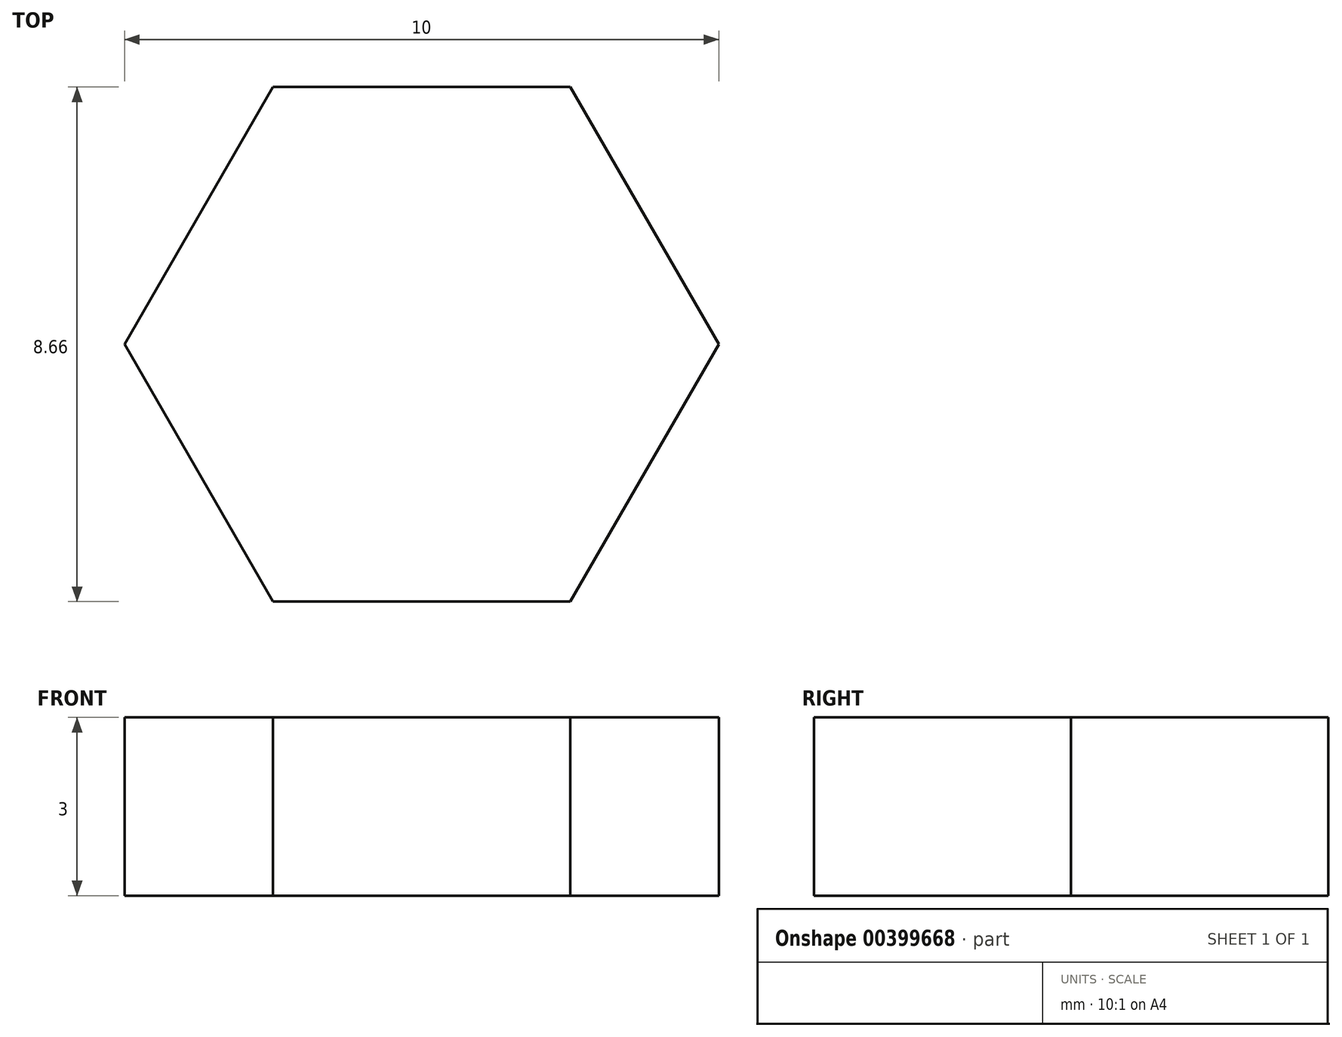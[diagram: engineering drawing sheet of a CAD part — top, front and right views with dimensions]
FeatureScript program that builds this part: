
annotation { "Feature Type Name" : "Feature", "Feature Type Description" : "" }
export const myFeature = defineFeature(function(context is Context, id is Id, definition is map)
    precondition{}
    {
        {
            var Q0;
            Q0=qCreatedBy(makeId("Top.planeOp"),FACE);
            var sketch = newSketch(context, id + "F0", { "sketchPlane" : qUnion([Q0])});
            skCircle(sketch, "E0.cCircle", {"center": v(0, 0) * mm, "radius": 4.33 * mm, "construction": true});
            skLineSegment(sketch, "E0.0", {"start": v(2.5, 4.33) * mm, "end": v(5, 0) * mm});
            skLineSegment(sketch, "E0.1", {"start": v(5, 0) * mm, "end": v(2.5, -4.33) * mm});
            skLineSegment(sketch, "E0.2", {"start": v(2.5, -4.33) * mm, "end": v(-2.5, -4.33) * mm});
            skLineSegment(sketch, "E0.3", {"start": v(-2.5, -4.33) * mm, "end": v(-5, 0) * mm});
            skLineSegment(sketch, "E0.4", {"start": v(-5, 0) * mm, "end": v(-2.5, 4.33) * mm});
            skLineSegment(sketch, "E0.5", {"start": v(-2.5, 4.33) * mm, "end": v(2.5, 4.33) * mm});
            skPoint(sketch, "E0.0.midPoint", {"position": v(3.75, 2.17) * mm});
            skSolve(sketch);
        }
        {
            var Q0;
            Q0=makeQuery(id+"F0.imprint","IMPRINT",FACE,{"disambiguationData":[TD([[makeQuery(id+"F0.imprint","IMPRINT",EDGE,{"derivedFrom":sQuery(id+"F0.wireOp",EDGE,"E0.0")}),-1.0]])]});
            extrude(context, id + "F1", {"entities" : qUnion([Q0]), "depth" : 3 * mm});
        }
    });
